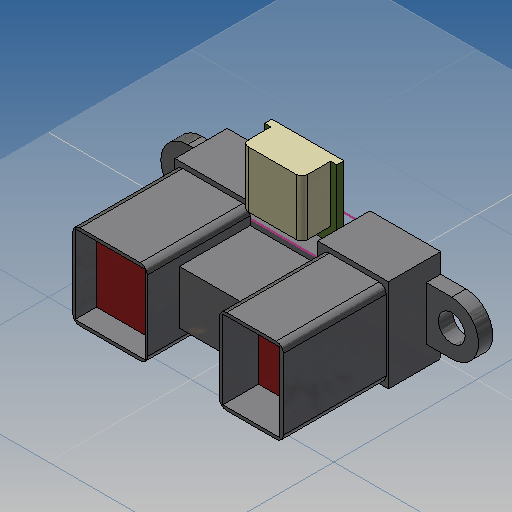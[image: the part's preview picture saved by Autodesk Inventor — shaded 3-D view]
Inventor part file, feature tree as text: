
AUTODESK INVENTOR PART (.ipt)
format: ipt  version: 2019 (Build 230136000, 136)  size: 510,464 bytes
history: native  units: mm
features: sketch x18, extrude x15, other x3, fillet x2
ambient origin geometry x8: Origin, YZ Plane, XZ Plane, XY Plane, X Axis, Y Axis, Z Axis, Center Point
bodies: Solid1 (feature_tree)
feature tree (38):
  sketch  "Sketch1"  dims[d0=37.0mm d1=13.0mm]
  extrude  "Extrusion1"  Depth=13.0mm
  extrude  "Extrusion2"  Depth=3.75mm
  extrude  "Extrusion3"  Depth=2.0mm TaperAngle=0.0deg
  extrude  "Extrusion4"  Depth=29.9mm
  extrude  "Extrusion5"  Depth=13.0mm
  extrude  "Extrusion6"  Depth=14.4mm
  extrude  "Extrusion7"  Depth=4.5mm TaperAngle=0.0deg
  extrude  "Extrusion8"  Depth=2.2mm TaperAngle=0.0deg
  extrude  "Extrusion9"  Depth=0.014mm TaperAngle=0.0deg
  extrude  "Extrusion10"  Depth=11.0mm
  extrude  "Extrusion11"  Depth=8.0mm
  sketch  "Sketch14"  dims[d142=5.05mm d143=10.1mm]
  extrude  "Extrusion12"  Depth=5.0mm TaperAngle=0.0deg
  extrude  "Extrusion13"  Depth=10.1mm
  extrude  "Extrusion14"  Depth=2.0mm TaperAngle=0.0deg
  sketch  "Sketch18"  dims[d154=4.0mm d155=0.0mm]
  extrude  "Extrusion15"  Depth=9.9mm TaperAngle=0.0deg
  fillet  "Fillet1"  Radius=29.0mm
  fillet  "Fillet2"  Radius=12.0mm
  sketch  "Sketch2"  dims[d30=3.75mm d31=3.75mm]
  other  "Image1"
  sketch  "Sketch3"  dims[d32=29.5mm d33=2.0mm d34=0.0mm]
  other  "Image3"
  sketch  "Sketch4"  dims[d46=14.95mm d48=29.9mm]
  other  "Image4"
  sketch  "Sketch6"  dims[d49=13.0mm d50=0.0mm d78=14.75mm]
  sketch  "Sketch7"  dims[d79=29.5mm d80=14.4mm]
  sketch  "Sketch8"  dims[d81=11.9mm d82=0.0mm d124=4.5mm d125=0.0mm]
  sketch  "Sketch9"  dims[d126=2.2mm d127=0.0mm d128=2.2mm d129=0.0mm]
  sketch  "Sketch10"  dims[d130=1.514mm d131=0.0mm d132=0.014mm d133=0.0mm]
  sketch  "Sketch11"  dims[d134=9.8mm d135=11.0mm]
  sketch  "Sketch12"  dims[d136=3.0mm d137=0.0mm d138=8.0mm]
  sketch  "Sketch13"  dims[d139=11.0mm d140=5.0mm d141=0.0mm]
  sketch  "Sketch15"  dims[d144=1.0mm d145=2.0mm d146=0.0mm]
  sketch  "Sketch16"  dims[d147=1.0mm d148=9.9mm d149=0.0mm d150=29.0mm d151=12.0mm]
  sketch  "Sketch17"  dims[d152=2.0mm d153=0.0mm]
  sketch  "Sketch19"  dims[d156=6.0mm d157=7.0mm d158=0.0mm d159=0.8mm d160=1.0mm]
